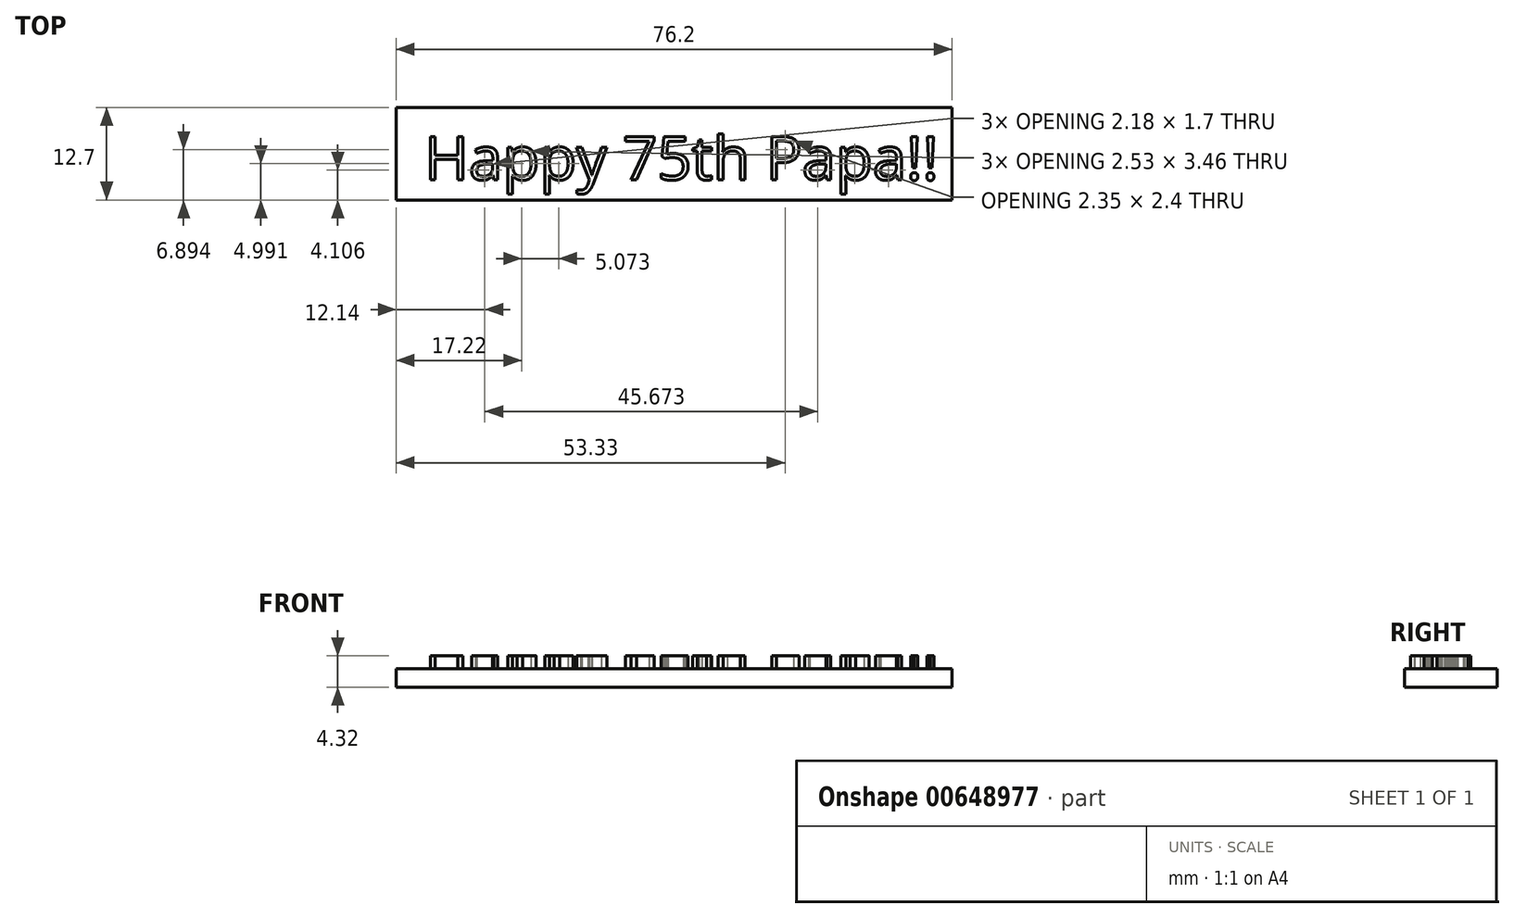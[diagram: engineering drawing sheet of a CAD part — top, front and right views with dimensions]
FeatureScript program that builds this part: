
annotation { "Feature Type Name" : "Feature", "Feature Type Description" : "" }
export const myFeature = defineFeature(function(context is Context, id is Id, definition is map)
    precondition{}
    {
        {
            var Q0;
            Q0=qCreatedBy(makeId("Top.planeOp"),FACE);
            var sketch = newSketch(context, id + "F0", { "sketchPlane" : qUnion([Q0])});
            skLineSegment(sketch, "E0.bottom", {"start": v(-3.86, 9.92) * mm, "end": v(72.34, 9.92) * mm});
            skLineSegment(sketch, "E0.top", {"start": v(-3.86, -2.78) * mm, "end": v(72.34, -2.78) * mm});
            skLineSegment(sketch, "E0.left", {"start": v(-3.86, 9.92) * mm, "end": v(-3.86, -2.78) * mm});
            skLineSegment(sketch, "E0.right", {"start": v(72.34, 9.92) * mm, "end": v(72.34, -2.78) * mm});
            skSolve(sketch);
        }
        {
            var Q0;
            Q0=makeQuery(id+"F0.imprint","IMPRINT",FACE,{"disambiguationData":[TD([[makeQuery(id+"F0.imprint","IMPRINT",EDGE,{"derivedFrom":sQuery(id+"F0.wireOp",EDGE,"E0.bottom")}),-1.0]])]});
            var sketch = newSketch(context, id + "F1", { "sketchPlane" : qUnion([Q0])});
            skText(sketch, "E1", { "text": "Happy 75th Papa!!", "fontName": "OpenSans-Regular.ttf"});
            const initialGuessF1  = {"E1": [0, 0, 1, 0, 0.00596]};
            skSetInitialGuess(sketch, initialGuessF1);
            skSolve(sketch);
        }
        {
            var Q0;
            Q0 = qSketchRegion(id + "F1", true);
            extrude(context, id + "F2", {"entities" : qUnion([Q0]), "depth" : 1.78 * mm, "offsetDistance" : 25.4 * mm});
        }
        {
            var Q0;
            Q0 = qSketchRegion(id + "F0", true);
            extrude(context, id + "F3", {"entities" : qUnion([Q0]), "oppositeDirection" : true, "depth" : 2.54 * mm, "offsetDistance" : 25.4 * mm});
        }
    });
